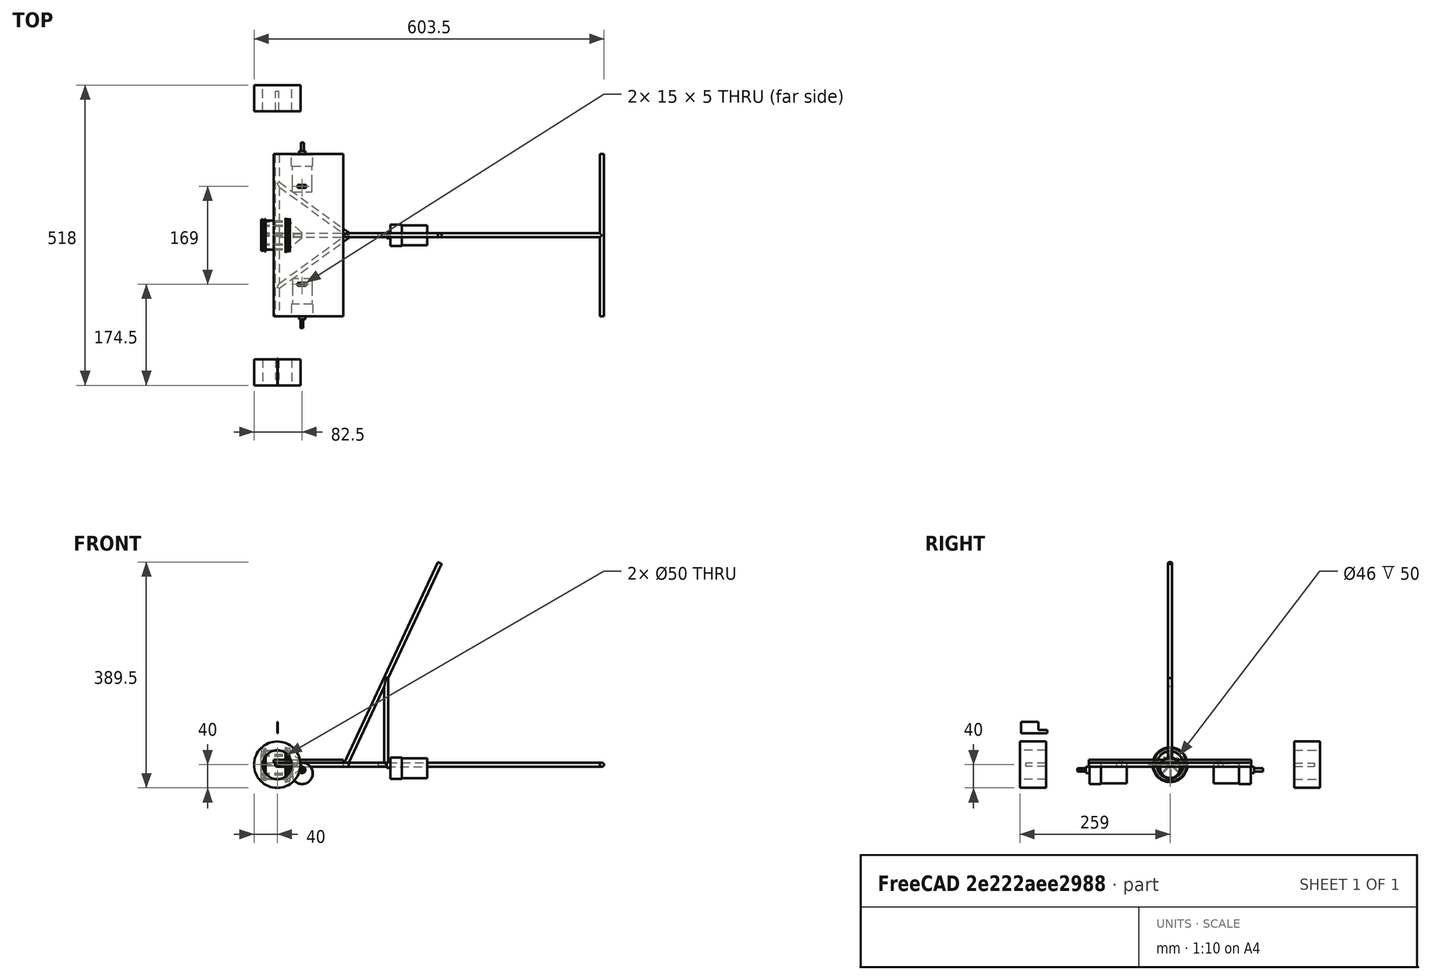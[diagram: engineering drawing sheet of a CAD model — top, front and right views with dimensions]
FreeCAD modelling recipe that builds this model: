
FCSTD DOCUMENT  (FreeCAD 0.16R6712 (Git))
Label: estructura exo
License: All rights reserved
LicenseURL: http://en.wikipedia.org/wiki/All_rights_reserved
objects: Part::Cylinder×37, Part::Box×13, Part::Cut×11, Part::MultiFuse×10, Part::Cone×1
note: 72 computed .brp shape members not serialized (recipe doc carries the construction recipe); baked Part::Feature solids carry a one-line shape summary decoded from their .brp

FEATURE [Part::Cylinder] Cylinder  label="Eje Central"
  Angle = 360
  Height = 560
  Placement = pos=(0,0,0) rot=(0,1,0;1.5708rad)
  Radius = 3.5
FEATURE [Part::Cylinder] Cylinder001  label="Eje Ruedas traseras"
  Angle = 360
  Height = 280
  Placement = pos=(0,140,0) rot=(1,0,0;1.5708rad)
  Radius = 3.5
FEATURE [Part::Cylinder] Cylinder002  label="Eje Ruedas delanteras"
  Angle = 360
  Height = 280
  Placement = pos=(560,140,0) rot=(1,0,0;1.5708rad)
  Radius = 3.5
FEATURE [Part::Cylinder] Cylinder003  label="Soporte Derecho"
  Angle = 360
  Height = 150
  Placement = pos=(0,-90,0) rot=(-0.295242,0.908661,0.295242;1.66643rad)
  Radius = 3.5
FEATURE [Part::Cylinder] Cylinder004  label="Soporte Izquierdo"
  Angle = 360
  Height = 150
  Placement = pos=(0,90,0) rot=(0.295242,0.908661,-0.295242;1.66643rad)
  Radius = 3.5
FEATURE [Part::Cylinder] Cylinder005  label="Soporte Mastil"
  Angle = 360
  Height = 150
  Placement = pos=(188,0,0) rot=(0,0,1;0rad)
  Radius = 3.5
FEATURE [Part::Cylinder] Cylinder006  label="Mastil"
  Angle = 360
  Height = 384
  Placement = pos=(118,0,0) rot=(0,1,0;0.436332rad)
  Radius = 3.5
FEATURE [Part::MultiFuse] Fusion  label="Estructura Exo"
  Shapes = -> [Cylinder,Cylinder001,Cylinder003,Cylinder002,Cylinder004,Cylinder005,Cylinder006]
FEATURE [Part::Box] Box  label="Tabla"
  Height = 5
  Length = 120
  Placement = pos=(-6,-140,73.5) rot=(0,0,1;0rad)
  Width = 280
FEATURE [Part::Cylinder] Cylinder012  label="Caja Reductora001"
  Angle = 360
  Height = 20
  Placement = pos=(0,-298,44) rot=(0,0,1;0rad)
  Radius = 18.4
FEATURE [Part::Cylinder] Cylinder013  label="Motor001"
  Angle = 360
  Height = 30
  Placement = pos=(0,-298,14) rot=(0,0,1;0rad)
  Radius = 17
FEATURE [Part::Cylinder] Cylinder014  label="Encoder001"
  Angle = 360
  Height = 14
  Placement = pos=(0,-298,0) rot=(0,0,1;0rad)
  Radius = 17
FEATURE [Part::Cylinder] Cylinder015  label="Cilindro002"
  Angle = 360
  Height = 6
  Placement = pos=(0,-292,64) rot=(0,0,1;0rad)
  Radius = 5.5
FEATURE [Part::Cylinder] Cylinder016  label="Cilindro003"
  Angle = 360
  Height = 15
  Placement = pos=(0,-186,0) rot=(0,0,1;0rad)
  Radius = 3
FEATURE [Part::Box] Box002  label="Cubo001"
  Height = 21
  Length = 11
  Placement = pos=(2,-191,-2) rot=(0,0,1;0rad)
  Width = 10
FEATURE [Part::Cut] Cut001
  Base = -> Cylinder016
  Placement = pos=(0,-106,70) rot=(0,0,1;0rad)
  Tool = -> Box002
FEATURE [Part::MultiFuse] Fusion002  label="Motor 37Dx68L001 Derecha"
  Placement = pos=(43,-75,283) rot=(1,0,0;1.5708rad)
  Shapes = -> [Cylinder012,Cylinder014,Cylinder015,Cylinder013,Cut001]
FEATURE [Part::Cylinder] Cylinder017  label="Caja Reductora002"
  Angle = 360
  Height = 20
  Placement = pos=(0,-298,44) rot=(0,0,1;0rad)
  Radius = 18.4
FEATURE [Part::Cylinder] Cylinder018  label="Motor002"
  Angle = 360
  Height = 30
  Placement = pos=(0,-298,14) rot=(0,0,1;0rad)
  Radius = 17
FEATURE [Part::Cylinder] Cylinder019  label="Encoder002"
  Angle = 360
  Height = 14
  Placement = pos=(0,-298,0) rot=(0,0,1;0rad)
  Radius = 17
FEATURE [Part::Cylinder] Cylinder020  label="Cilindro004"
  Angle = 360
  Height = 6
  Placement = pos=(0,-292,64) rot=(0,0,1;0rad)
  Radius = 5.5
FEATURE [Part::Cylinder] Cylinder021  label="Cilindro005"
  Angle = 360
  Height = 15
  Placement = pos=(0,-186,0) rot=(0,0,1;0rad)
  Radius = 3
FEATURE [Part::Box] Box003  label="Cubo002"
  Height = 21
  Length = 11
  Placement = pos=(2,-191,-2) rot=(0,0,1;0rad)
  Width = 10
FEATURE [Part::Cut] Cut002
  Base = -> Cylinder021
  Placement = pos=(0,-106,70) rot=(0,0,1;0rad)
  Tool = -> Box003
FEATURE [Part::MultiFuse] Fusion003  label="Motor 37Dx68L001 Izquierda001"
  Placement = pos=(43,75,283) rot=(0,0.707107,0.707107;3.14159rad)
  Shapes = -> [Cylinder017,Cylinder019,Cylinder020,Cylinder018,Cut002]
FEATURE [Part::Box] Box004  label="Cubo003"
  Height = 16
  Length = 15
  Placement = pos=(35,-87,68) rot=(0,0,1;0rad)
  Width = 5
FEATURE [Part::Cut] Cut003
  Base = -> Box
  Tool = -> Box004
FEATURE [Part::Box] Box005  label="Cubo004"
  Height = 16
  Length = 15
  Placement = pos=(35,82,69) rot=(0,0,1;0rad)
  Width = 5
FEATURE [Part::Cut] Cut004  label="Tabla Cortes"
  Base = -> Cut003
  Placement = pos=(0,0,-70) rot=(0,0,1;0rad)
  Tool = -> Box005
FEATURE [Part::Cylinder] Cylinder022  label="Cilindro"
  Angle = 360
  Height = 45
  Placement = pos=(0,-214,0) rot=(1,0,0;1.5708rad)
  Radius = 40
FEATURE [Part::Cylinder] Cylinder023  label="Cilindro006"
  Angle = 360
  Height = 60
  Placement = pos=(0,-207,0) rot=(1,0,0;1.5708rad)
  Radius = 25
FEATURE [Part::Cut] Cut
  Base = -> Cylinder022
  Tool = -> Cylinder023
FEATURE [Part::Cylinder] Cylinder024  label="Cilindro007"
  Angle = 360
  Height = 35
  Placement = pos=(0,-214,0) rot=(1,0,0;1.5708rad)
  Radius = 3
FEATURE [Part::MultiFuse] Fusion004  label="Rueda Derecha"
  Shapes = -> [Cut,Cylinder024]
FEATURE [Part::Cylinder] Cylinder025  label="Cilindro008"
  Angle = 360
  Height = 45
  Placement = pos=(0,-214,0) rot=(1,0,0;1.5708rad)
  Radius = 40
FEATURE [Part::Cylinder] Cylinder026  label="Cilindro009"
  Angle = 360
  Height = 60
  Placement = pos=(0,-207,0) rot=(1,0,0;1.5708rad)
  Radius = 25
FEATURE [Part::Cut] Cut005
  Base = -> Cylinder025
  Tool = -> Cylinder026
FEATURE [Part::Cylinder] Cylinder027  label="Cilindro010"
  Angle = 360
  Height = 35
  Placement = pos=(0,-214,0) rot=(1,0,0;1.5708rad)
  Radius = 3
FEATURE [Part::MultiFuse] Fusion005  label="Rueda Izquierda"
  Placement = pos=(0,0,0) rot=(0,0,1;3.14159rad)
  Shapes = -> [Cut005,Cylinder027]
FEATURE [Part::Box] Box006  label="Cubo"
  Height = 20
  Length = 1
  Placement = pos=(0,-257,54) rot=(0,0,1;0rad)
  Width = 45
FEATURE [Part::Box] Box007  label="Cubo005"
  Height = 14
  Length = 10
  Placement = pos=(-4,-227,60) rot=(0,0,1;0rad)
  Width = 15
FEATURE [Part::Cut] Cut006
  Base = -> Box006
  Tool = -> Box007
FEATURE [Part::Cylinder] Cylinder028  label="Caja Reductora003"
  Angle = 360
  Height = 20
  Placement = pos=(0,-298,44) rot=(0,0,1;0rad)
  Radius = 18.4
FEATURE [Part::Cylinder] Cylinder029  label="Motor003"
  Angle = 360
  Height = 30
  Placement = pos=(0,-298,14) rot=(0,0,1;0rad)
  Radius = 17
FEATURE [Part::Cylinder] Cylinder030  label="Encoder003"
  Angle = 360
  Height = 14
  Placement = pos=(0,-298,0) rot=(0,0,1;0rad)
  Radius = 17
FEATURE [Part::Cylinder] Cylinder031  label="Cilindro011"
  Angle = 360
  Height = 6
  Placement = pos=(0,-292,64) rot=(0,0,1;0rad)
  Radius = 5.5
FEATURE [Part::Cylinder] Cylinder032  label="Cilindro012"
  Angle = 360
  Height = 15
  Placement = pos=(0,-186,0) rot=(0,0,1;0rad)
  Radius = 3
FEATURE [Part::Box] Box008  label="Cubo006"
  Height = 21
  Length = 11
  Placement = pos=(2,-191,-2) rot=(0,0,1;0rad)
  Width = 10
FEATURE [Part::Cut] Cut007
  Base = -> Cylinder032
  Placement = pos=(0,-106,70) rot=(0,0,1;0rad)
  Tool = -> Box008
FEATURE [Part::MultiFuse] Fusion006  label="Motor 37Dx68L001 Derecha001"
  Placement = pos=(259,0,292) rot=(0.57735,-0.57735,-0.57735;2.0944rad)
  Shapes = -> [Cylinder028,Cylinder030,Cylinder031,Cylinder029,Cut007]
FEATURE [Part::Cylinder] Cylinder033  label="Cilindro013"
  Angle = 360
  Height = 4
  Placement = pos=(0,0,0) rot=(0,1,0;1.5708rad)
  Radius = 29
FEATURE [Part::Cylinder] Cylinder034  label="Cilindro014"
  Angle = 360
  Height = 2
  Placement = pos=(-2,0,0) rot=(0,1,0;1.5708rad)
  Radius = 26
FEATURE [Part::Cylinder] Cylinder035  label="Cilindro015"
  Angle = 360
  Height = 2
  Placement = pos=(-4,0,0) rot=(0,1,0;1.5708rad)
  Radius = 30
FEATURE [Part::MultiFuse] Fusion007  label="Riel Derecho"
  Placement = pos=(18,0,0) rot=(0,0,1;0rad)
  Shapes = -> [Cylinder033,Cylinder035,Cylinder034]
FEATURE [Part::Cylinder] Cylinder036  label="Cilindro016"
  Angle = 360
  Height = 4
  Placement = pos=(0,0,0) rot=(0,1,0;1.5708rad)
  Radius = 27
FEATURE [Part::Cylinder] Cylinder037  label="Cilindro017"
  Angle = 360
  Height = 2
  Placement = pos=(-2,0,0) rot=(0,1,0;1.5708rad)
  Radius = 25
FEATURE [Part::Cylinder] Cylinder038  label="Cilindro018"
  Angle = 360
  Height = 2
  Placement = pos=(-4,0,0) rot=(0,1,0;1.5708rad)
  Radius = 28
FEATURE [Part::MultiFuse] Fusion008  label="Riel Izquierdo"
  Placement = pos=(-24,0,0) rot=(0,1,0;3.14159rad)
  Shapes = -> [Cylinder036,Cylinder038,Cylinder037]
FEATURE [Part::Cylinder] Cylinder039  label="Centro"
  Angle = 360
  Height = 34
  Placement = pos=(-20,0,0) rot=(0,1,0;1.5708rad)
  Radius = 25
FEATURE [Part::Cylinder] Cylinder040  label="Corte"
  Angle = 360
  Height = 50
  Placement = pos=(-28,0,0) rot=(0,1,0;1.5708rad)
  Radius = 23
FEATURE [Part::MultiFuse] Fusion009  label="Rin Solido"
  Shapes = -> [Fusion007,Cylinder039,Fusion008]
FEATURE [Part::Cut] Cut008  label="Rin"
  Base = -> Fusion009
  Tool = -> Cylinder040
FEATURE [Part::Cone] Cone  label="Cono"
  Angle = 360
  Height = 20
  Placement = pos=(100,0,0) rot=(0,-1,0;1.5708rad)
  Radius1 = 5
  Radius2 = 23
FEATURE [Part::Cylinder] Cylinder041  label="Cilindro019"
  Angle = 360
  Height = 15
  Placement = pos=(0,-186,0) rot=(0,0,1;0rad)
  Radius = 3
FEATURE [Part::Box] Box009  label="Cubo007"
  Height = 21
  Length = 11
  Placement = pos=(2,-191,-2) rot=(0,0,1;0rad)
  Width = 10
FEATURE [Part::Cut] Cut009
  Base = -> Cylinder041
  Placement = pos=(86,186,0) rot=(0,1,0;1.5708rad)
  Tool = -> Box009
FEATURE [Part::Cut] Cut010  label="Cono Rin"
  Base = -> Cone
  Placement = pos=(-58,0,0) rot=(0,0,1;0rad)
  Tool = -> Cut009
FEATURE [Part::Box] Box010  label="Cubo008"
  Height = 46
  Length = 50
  Placement = pos=(-28,0,-23) rot=(0,0,1;0rad)
  Width = 2
FEATURE [Part::Box] Box011  label="Cubo009"
  Height = 46
  Length = 50
  Placement = pos=(-28,23,0) rot=(1,0,0;1.5708rad)
  Width = 2
FEATURE [Part::Box] Box012  label="Cubo010"
  Height = 46
  Length = 50
  Placement = pos=(-28,16.5,-16) rot=(1,0,0;0.785398rad)
  Width = 2
FEATURE [Part::Box] Box013  label="Cubo011"
  Height = 46
  Length = 50
  Placement = pos=(-28,-16.5,-16) rot=(-1,0,0;0.785398rad)
  Width = 2
FEATURE [Part::MultiFuse] Fusion010  label="Soporte interno"
  Shapes = -> [Box010,Box012,Box013,Box011]
